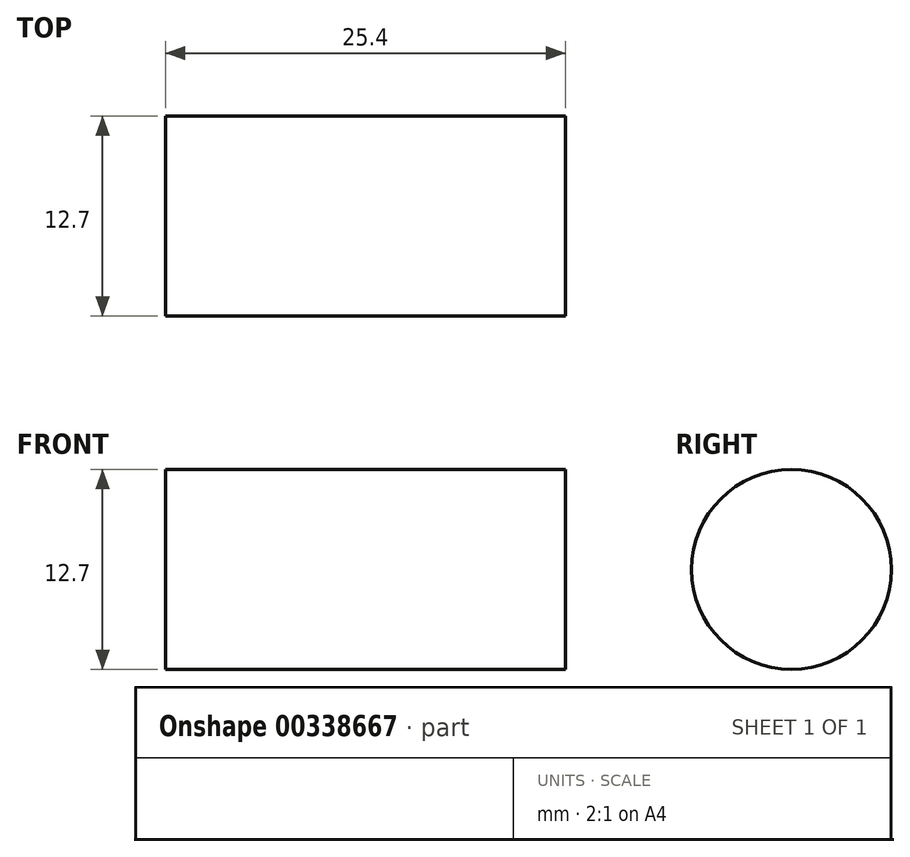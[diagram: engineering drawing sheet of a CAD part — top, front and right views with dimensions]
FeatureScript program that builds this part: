
annotation { "Feature Type Name" : "Feature", "Feature Type Description" : "" }
export const myFeature = defineFeature(function(context is Context, id is Id, definition is map)
    precondition{}
    {
        {
            var Q0;
            Q0=qCreatedBy(makeId("Right.planeOp"),FACE);
            var sketch = newSketch(context, id + "F0", { "sketchPlane" : qUnion([Q0])});
            skCircle(sketch, "E0", {"center": v(0, 0) * mm, "radius": 6.35 * mm});
            skSolve(sketch);
        }
        {
            var Q0;
            Q0=makeQuery(id+"F0.imprint","IMPRINT",FACE,{"disambiguationData":[TD([[makeQuery(id+"F0.imprint","IMPRINT",EDGE,{"derivedFrom":sQuery(id+"F0.wireOp",EDGE,"E0")}),1.0]])]});
            var Q1;
            Q1=sQuery(id+"F0.wireOp",EDGE,"E0");
            extrude(context, id + "F1", {"entities" : qUnion([Q0]), "surfaceEntities" : qUnion([Q1]), "depth" : 25.4 * mm});
        }
    });
